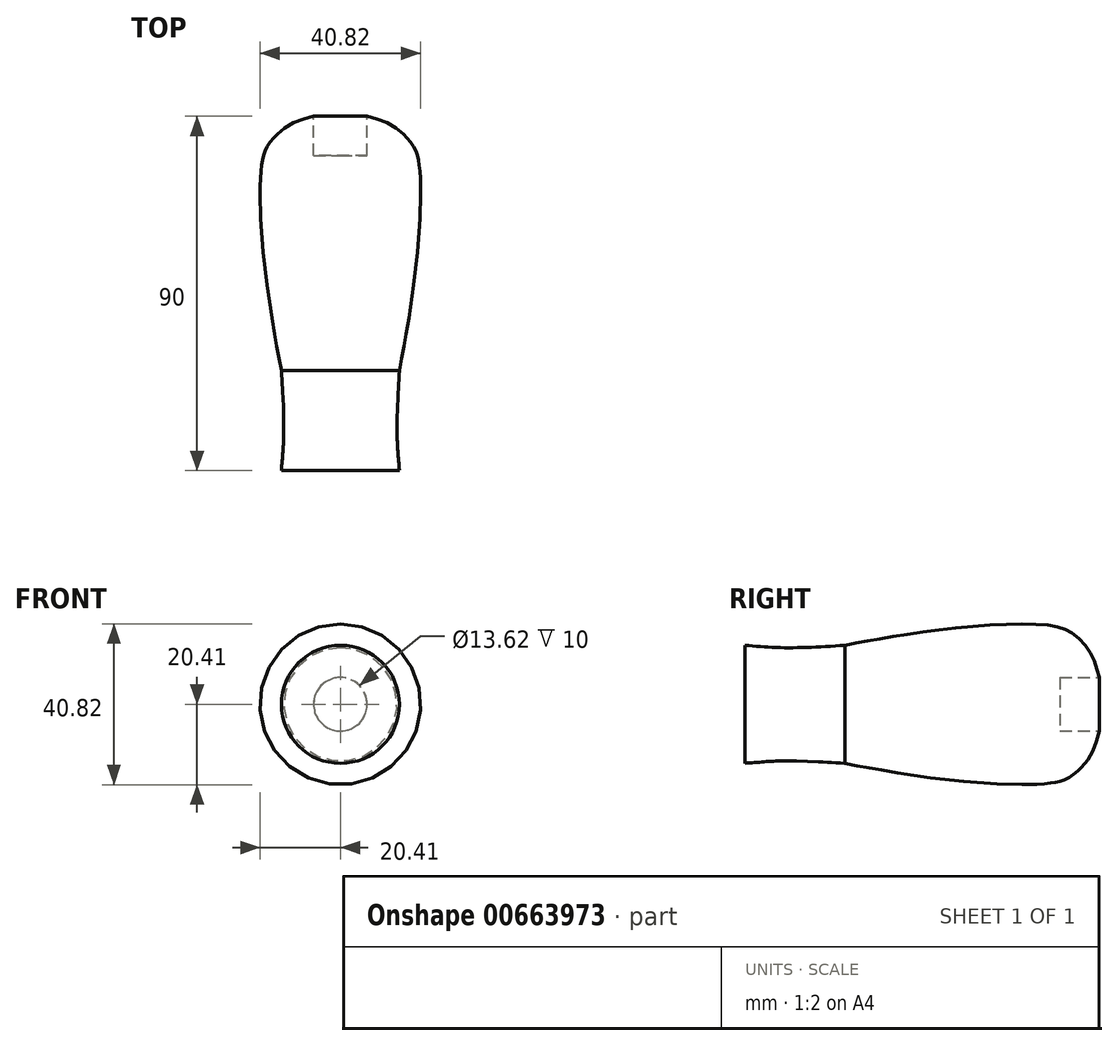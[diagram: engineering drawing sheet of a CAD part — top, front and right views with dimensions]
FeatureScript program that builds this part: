
annotation { "Feature Type Name" : "Feature", "Feature Type Description" : "" }
export const myFeature = defineFeature(function(context is Context, id is Id, definition is map)
    precondition{}
    {
        {
            var Q0;
            Q0=qCreatedBy(makeId("Top.planeOp"),FACE);
            var sketch = newSketch(context, id + "F0", { "sketchPlane" : qUnion([Q0])});
            skPoint(sketch, "E0.middle", {"position": v(0, 0) * mm});
            skLineSegment(sketch, "E1", {"start": v(0, 30) * mm, "end": v(0, -60) * mm});
            skLineSegment(sketch, "E2", {"start": v(0, 30) * mm, "end": v(-6.81, 30) * mm});
            skFitSpline(sketch, "E3", {"points": [v(-6.81, 30) * mm, v(-12.78, 27.9) * mm, v(-18, 23.23) * mm, v(-20, 17.82) * mm, v(-20, 0) * mm, v(-17.26, -22.11) * mm, v(-15, -34.62) * mm], "startDerivative": vector(-48.27, -12.1) * mm, "endDerivative": vector(12.46, -65.1) * mm});
            skFitSpline(sketch, "E4", {"points": [v(-15, -34.62) * mm, v(-14.37, -49.37) * mm, v(-15, -60) * mm], "startDerivative": vector(1.84, -28.4) * mm, "endDerivative": vector(-1.94, -22.2) * mm});
            skLineSegment(sketch, "E5", {"start": v(-15, -60) * mm, "end": v(0, -60) * mm});
            skSolve(sketch);
        }
        {
            var Q0;
            Q0 = qSketchRegion(id + "F0", true);
            var Q1;
            Q1=sQuery(id+"F0.wireOp",EDGE,"E1");
            revolve(context, id + "F1", {"entities" : qUnion([Q0]), "axis" : qUnion([Q1]), "revolveType" : RevolveType.FULL});
        }
        {
            var Q0;
            Q0=makeQuery(id+"F1.opRevolve","SWEPT_FACE",FACE,{"disambiguationData":[OSD([sQuery(id+"F0.wireOp",EDGE,"E2")])]});
            var sketch = newSketch(context, id + "F2", { "sketchPlane" : qUnion([Q0])});
            skCircle(sketch, "E6", {"center": v(0, 0) * mm, "radius": 6.81 * mm});
            skSolve(sketch);
        }
        {
            var Q0;
            Q0 = qSketchRegion(id + "F2", true);
            extrude(context, id + "F3", {"entities" : qUnion([Q0]), "operationType" : NewBodyOperationType.REMOVE, "oppositeDirection" : true, "depth" : 10 * mm, "offsetDistance" : 25 * mm});
        }
    });
